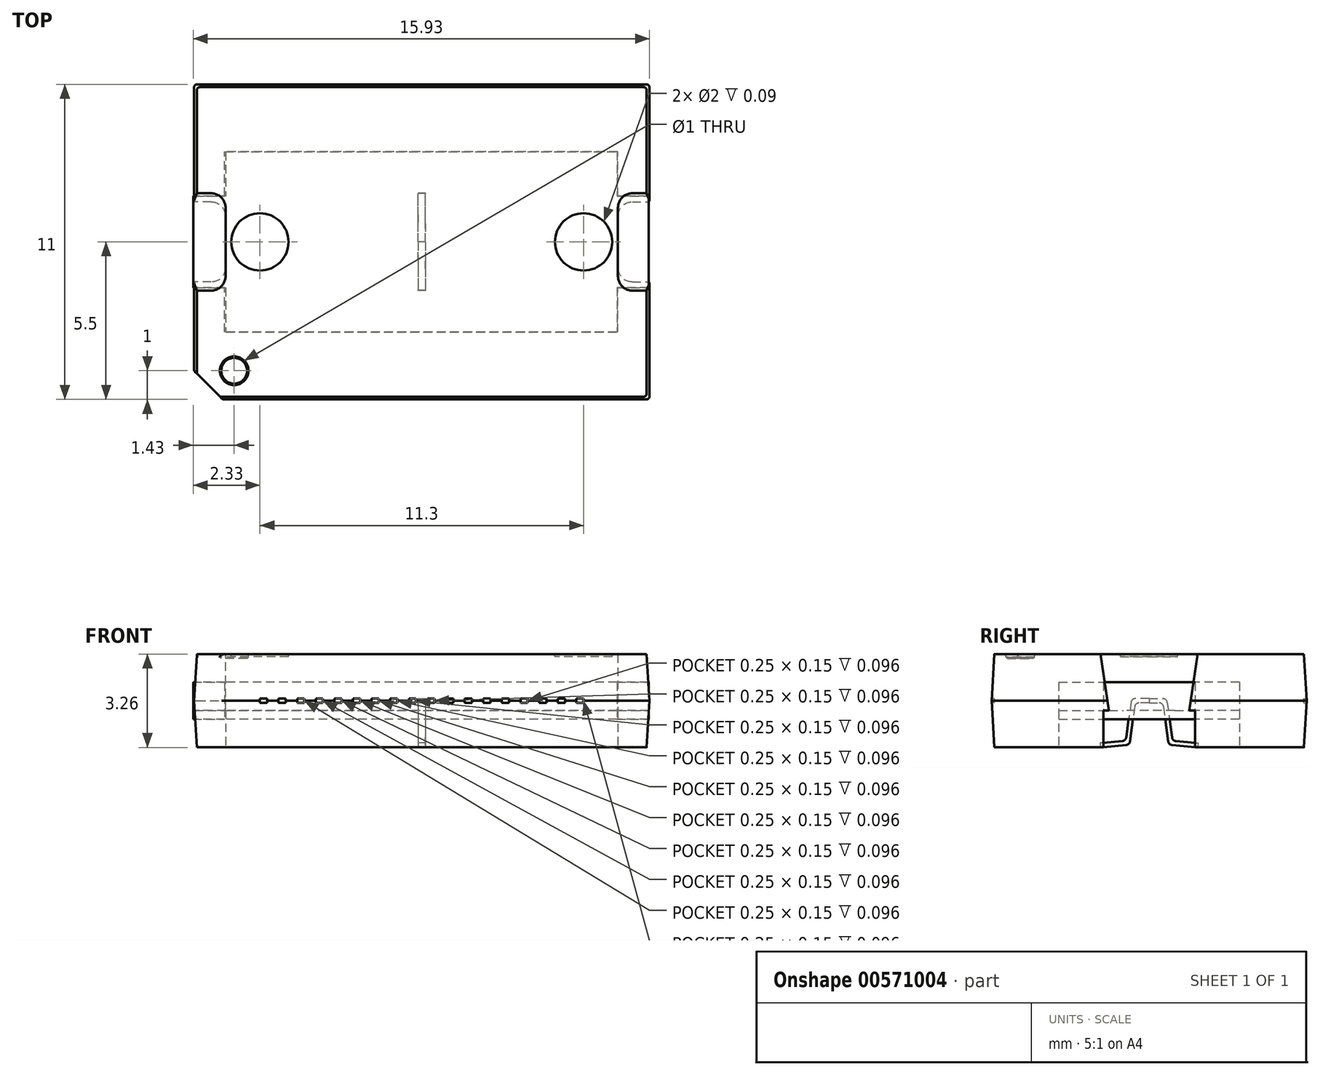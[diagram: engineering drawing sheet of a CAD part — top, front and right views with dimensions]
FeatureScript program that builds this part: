
annotation { "Feature Type Name" : "Feature", "Feature Type Description" : "" }
export const myFeature = defineFeature(function(context is Context, id is Id, definition is map)
    precondition{}
    {
        {
            var Q0;
            Q0=qCreatedBy(makeId("Top.planeOp"),FACE);
            var sketch = newSketch(context, id + "F0", { "sketchPlane" : qUnion([Q0])});
            skLineSegment(sketch, "E0.bottom", {"start": v(-7.95, 5.5) * mm, "end": v(7.95, 5.5) * mm});
            skLineSegment(sketch, "E0.top", {"start": v(-7.95, -5.5) * mm, "end": v(7.95, -5.5) * mm});
            skLineSegment(sketch, "E0.left", {"start": v(-7.95, 5.5) * mm, "end": v(-7.95, -5.5) * mm});
            skLineSegment(sketch, "E0.right", {"start": v(7.95, 5.5) * mm, "end": v(7.95, -5.5) * mm});
            skPoint(sketch, "E0.middle", {"position": v(0, 0) * mm});
            skLineSegment(sketch, "E1", {"start": v(-6.95, -5.5) * mm, "end": v(-7.95, -4.5) * mm});
            skLineSegment(sketch, "E2", {"start": v(-7.95, 1.4) * mm, "end": v(-6.85, 1.4) * mm});
            skLineSegment(sketch, "E3", {"start": v(-6.85, 1.4) * mm, "end": v(-6.85, -1.4) * mm});
            skLineSegment(sketch, "E4", {"start": v(-6.85, -1.4) * mm, "end": v(-7.95, -1.4) * mm});
            skLineSegment(sketch, "E5.MirrorCS", {"start": v(7.95, 1.4) * mm, "end": v(6.85, 1.4) * mm});
            skLineSegment(sketch, "E6.MirrorCS", {"start": v(6.85, 1.4) * mm, "end": v(6.85, -1.4) * mm});
            skLineSegment(sketch, "E7.MirrorCS", {"start": v(6.85, -1.4) * mm, "end": v(7.95, -1.4) * mm});
            skLineSegment(sketch, "E8", {"start": v(6.85, 2.95) * mm, "end": v(6.85, 1.6) * mm});
            skLineSegment(sketch, "E9", {"start": v(6.85, 2.95) * mm, "end": v(0, 2.95) * mm});
            skLineSegment(sketch, "E10", {"start": v(6.85, 1.6) * mm, "end": v(7.95, 1.6) * mm});
            skLineSegment(sketch, "E11", {"start": v(0, -2.95) * mm, "end": v(6.85, -2.95) * mm});
            skLineSegment(sketch, "E12", {"start": v(6.85, -2.95) * mm, "end": v(6.85, -1.6) * mm});
            skLineSegment(sketch, "E13", {"start": v(6.85, -1.6) * mm, "end": v(7.95, -1.6) * mm});
            skLineSegment(sketch, "E14.MirrorCS", {"start": v(-6.85, 2.95) * mm, "end": v(0, 2.95) * mm});
            skLineSegment(sketch, "E15.MirrorCS", {"start": v(-6.85, 2.95) * mm, "end": v(-6.85, 1.6) * mm});
            skLineSegment(sketch, "E16.MirrorCS", {"start": v(-6.85, 1.6) * mm, "end": v(-7.95, 1.6) * mm});
            skLineSegment(sketch, "E17.MirrorCS", {"start": v(0, -2.95) * mm, "end": v(-6.85, -2.95) * mm});
            skLineSegment(sketch, "E18.MirrorCS", {"start": v(-6.85, -1.6) * mm, "end": v(-7.95, -1.6) * mm});
            skLineSegment(sketch, "E19.MirrorCS", {"start": v(-6.85, -2.95) * mm, "end": v(-6.85, -1.6) * mm});
            skSolve(sketch);
        }
        {
            var Q0;
            {var subQ1=sQuery(id+"F0.wireOp",EDGE,"E0.bottom");Q0=makeQuery(id+"F0.imprint","IMPRINT",FACE,{"disambiguationData":[TD([[makeQuery(id+"F0.imprint","IMPRINT",EDGE,{"derivedFrom":subQ1}),-1.0]])]});}
            var Q1;
            {var subQ0=sQuery(id+"F0.wireOp",EDGE,"E1");Q1=makeQuery(id+"F0.imprint","IMPRINT",FACE,{"disambiguationData":[TD([[makeQuery(id+"F0.imprint","IMPRINT",EDGE,{"derivedFrom":subQ0}),-1.0]])]});}
            var Q2;
            {var subQ2=sQuery(id+"F0.wireOp",EDGE,"E2");Q2=makeQuery(id+"F0.imprint","IMPRINT",FACE,{"disambiguationData":[TD([[makeQuery(id+"F0.imprint","IMPRINT",EDGE,{"derivedFrom":subQ2}),1.0]])]});}
            var Q3;
            {var subQ0=sQuery(id+"F0.wireOp",EDGE,"E2");Q3=makeQuery(id+"F0.imprint","IMPRINT",FACE,{"disambiguationData":[TD([[makeQuery(id+"F0.imprint","IMPRINT",EDGE,{"derivedFrom":subQ0}),-1.0]])]});}
            var Q4;
            {var subQ0=sQuery(id+"F0.wireOp",EDGE,"E5.MirrorCS");Q4=makeQuery(id+"F0.imprint","IMPRINT",FACE,{"disambiguationData":[TD([[makeQuery(id+"F0.imprint","IMPRINT",EDGE,{"derivedFrom":subQ0}),1.0]])]});}
            extrude(context, id + "F1", {"entities" : qUnion([Q0, Q1, Q2, Q3, Q4]), "endBound" : BoundingType.SYMMETRIC, "depth" : 3.25 * mm, "offsetDistance" : 25 * mm});
        }
        {
            var Q0;
            Q0=makeQuery(id+"F1.opExtrude","CAP_FACE",FACE,{"disambiguationData":[OSD([sQuery(id+"F0.wireOp",EDGE,"E0.bottom"),sQuery(id+"F0.wireOp",EDGE,"E0.top"),sQuery(id+"F0.wireOp",EDGE,"E0.left"),sQuery(id+"F0.wireOp",EDGE,"E0.right"),sQuery(id+"F0.wireOp",EDGE,"E1")])],"isStart":true});
            var sketch = newSketch(context, id + "F2", { "sketchPlane" : qUnion([Q0])});
            skLineSegment(sketch, "E20", {"start": v(-6.85, -1.6) * mm, "end": v(-7.95, -1.6) * mm});
            skLineSegment(sketch, "E21", {"start": v(-7.95, -1.6) * mm, "end": v(-7.95, 1.6) * mm});
            skLineSegment(sketch, "E22", {"start": v(-7.95, 1.6) * mm, "end": v(-6.84, 1.6) * mm});
            skLineSegment(sketch, "E23", {"start": v(-6.84, 1.6) * mm, "end": v(-6.84, 3.15) * mm});
            skLineSegment(sketch, "E24", {"start": v(-6.84, 3.15) * mm, "end": v(0, 3.15) * mm});
            skLineSegment(sketch, "E25", {"start": v(0, 3.15) * mm, "end": v(6.85, 3.15) * mm});
            skPoint(sketch, "E25.endSnap0", {"position": v(-3.42, 3.15) * mm});
            skLineSegment(sketch, "E26", {"start": v(6.85, 3.15) * mm, "end": v(6.85, 1.6) * mm});
            skLineSegment(sketch, "E27", {"start": v(6.85, 1.6) * mm, "end": v(7.95, 1.6) * mm});
            skLineSegment(sketch, "E28", {"start": v(7.95, 1.6) * mm, "end": v(7.95, -1.6) * mm});
            skLineSegment(sketch, "E29", {"start": v(7.95, -1.6) * mm, "end": v(6.85, -1.6) * mm});
            skLineSegment(sketch, "E30", {"start": v(6.85, -1.6) * mm, "end": v(6.85, -3.15) * mm});
            skLineSegment(sketch, "E31", {"start": v(6.85, -3.15) * mm, "end": v(-6.85, -3.15) * mm});
            skLineSegment(sketch, "E32", {"start": v(-6.85, -3.15) * mm, "end": v(-6.85, -1.6) * mm});
            skSolve(sketch);
        }
        {
            var Q0;
            Q0=makeQuery(id+"F2.imprint","IMPRINT",FACE,{"disambiguationData":[TD([[makeQuery(id+"F2.imprint","IMPRINT",EDGE,{"derivedFrom":sQuery(id+"F2.wireOp",EDGE,"E20")}),-1.0]])]});
            extrude(context, id + "F3", {"entities" : qUnion([Q0]), "operationType" : NewBodyOperationType.REMOVE, "oppositeDirection" : true, "depth" : 1.29 * mm, "offsetDistance" : 25 * mm});
        }
        {
            var Q0;
            Q0=makeQuery(id+"F1.opExtrude","SWEPT_FACE",FACE,{"disambiguationData":[OSD([sQuery(id+"F0.wireOp",EDGE,"E0.right")])]});
            var sketch = newSketch(context, id + "F4", { "sketchPlane" : qUnion([Q0])});
            skLineSegment(sketch, "E33", {"start": v(0, -0.34) * mm, "end": v(0, 1.63) * mm});
            skLineSegment(sketch, "E34", {"start": v(0, 1.63) * mm, "end": v(-1.7, 1.63) * mm});
            skLineSegment(sketch, "E35", {"start": v(-1.7, 1.63) * mm, "end": v(-1.4, -0.34) * mm});
            skLineSegment(sketch, "E36", {"start": v(-1.4, -0.34) * mm, "end": v(0, -0.34) * mm});
            skLineSegment(sketch, "E37.MirrorCS", {"start": v(1.7, 1.63) * mm, "end": v(1.4, -0.34) * mm});
            skLineSegment(sketch, "E38.MirrorCS", {"start": v(0, 1.63) * mm, "end": v(1.7, 1.63) * mm});
            skLineSegment(sketch, "E39.MirrorCS", {"start": v(1.4, -0.34) * mm, "end": v(0, -0.34) * mm});
            skSolve(sketch);
        }
        {
            var Q0;
            Q0=makeQuery(id+"F4.imprint","IMPRINT",FACE,{"disambiguationData":[TD([[makeQuery(id+"F4.imprint","IMPRINT",EDGE,{"derivedFrom":sQuery(id+"F4.wireOp",EDGE,"E33")}),1.0]])]});
            var Q1;
            Q1=makeQuery(id+"F4.imprint","IMPRINT",FACE,{"disambiguationData":[TD([[makeQuery(id+"F4.imprint","IMPRINT",EDGE,{"derivedFrom":sQuery(id+"F4.wireOp",EDGE,"E33")}),-1.0]])]});
            extrude(context, id + "F5", {"entities" : qUnion([Q0, Q1]), "operationType" : NewBodyOperationType.REMOVE, "oppositeDirection" : true, "depth" : 1.1 * mm, "offsetDistance" : 25 * mm});
        }
        {
            var Q0;
            Q0=makeQuery(id+"F1.opExtrude","SWEPT_FACE",FACE,{"disambiguationData":[OSD([sQuery(id+"F0.wireOp",EDGE,"E0.left")])]});
            var sketch = newSketch(context, id + "F6", { "sketchPlane" : qUnion([Q0])});
            skLineSegment(sketch, "E40", {"start": v(0, -0.33) * mm, "end": v(-1.4, -0.34) * mm});
            skLineSegment(sketch, "E41", {"start": v(-1.4, -0.34) * mm, "end": v(-1.7, 1.63) * mm});
            skLineSegment(sketch, "E42", {"start": v(-1.7, 1.63) * mm, "end": v(0, 1.63) * mm});
            skLineSegment(sketch, "E43.MirrorCS", {"start": v(1.4, -0.34) * mm, "end": v(1.7, 1.63) * mm});
            skLineSegment(sketch, "E44.MirrorCS", {"start": v(1.7, 1.63) * mm, "end": v(0, 1.63) * mm});
            skLineSegment(sketch, "E45.MirrorCS", {"start": v(0, -0.33) * mm, "end": v(1.4, -0.34) * mm});
            skSolve(sketch);
        }
        {
            var Q0;
            Q0=makeQuery(id+"F6.imprint","IMPRINT",FACE,{"disambiguationData":[TD([[makeQuery(id+"F6.imprint","IMPRINT",EDGE,{"derivedFrom":sQuery(id+"F6.wireOp",EDGE,"E40")}),1.0]])]});
            extrude(context, id + "F7", {"entities" : qUnion([Q0]), "operationType" : NewBodyOperationType.REMOVE, "oppositeDirection" : true, "depth" : 1.1 * mm, "offsetDistance" : 25 * mm});
        }
        {
            var Q0;
            Q0=makeQuery(id+"F1.opExtrude","CAP_FACE",FACE,{"disambiguationData":[OSD([sQuery(id+"F0.wireOp",EDGE,"E0.bottom"),sQuery(id+"F0.wireOp",EDGE,"E0.top"),sQuery(id+"F0.wireOp",EDGE,"E0.left"),sQuery(id+"F0.wireOp",EDGE,"E0.right"),sQuery(id+"F0.wireOp",EDGE,"E1")])],"isStart":false});
            var sketch = newSketch(context, id + "F8", { "sketchPlane" : qUnion([Q0])});
            skCircle(sketch, "E46", {"center": v(-6.55, -4.5) * mm, "radius": 0.5 * mm});
            skCircle(sketch, "E47", {"center": v(-5.65, 0) * mm, "radius": 1 * mm});
            skPoint(sketch, "E47.centerSnap0", {"position": v(-6.85, 0) * mm});
            skCircle(sketch, "E48", {"center": v(5.65, 0) * mm, "radius": 1 * mm});
            skSolve(sketch);
        }
        {
            var Q0;
            Q0=makeQuery(id+"F8.imprint","IMPRINT",FACE,{"disambiguationData":[TD([[makeQuery(id+"F8.imprint","IMPRINT",EDGE,{"derivedFrom":sQuery(id+"F8.wireOp",EDGE,"E47")}),1.0]])]});
            var Q1;
            Q1=makeQuery(id+"F8.imprint","IMPRINT",FACE,{"disambiguationData":[TD([[makeQuery(id+"F8.imprint","IMPRINT",EDGE,{"derivedFrom":sQuery(id+"F8.wireOp",EDGE,"E48")}),1.0]])]});
            extrude(context, id + "F9", {"entities" : qUnion([Q0, Q1]), "operationType" : NewBodyOperationType.REMOVE, "oppositeDirection" : true, "depth" : 0.09 * mm, "offsetDistance" : 25 * mm});
        }
        {
            var Q0;
            Q0=makeQuery(id+"F1.opExtrude","SWEPT_FACE",FACE,{"disambiguationData":[OSD([sQuery(id+"F0.wireOp",EDGE,"E0.top")])]});
            var sketch = newSketch(context, id + "F10", { "sketchPlane" : qUnion([Q0])});
            skLineSegment(sketch, "E49.bottom", {"start": v(-0.45, 0.07) * mm, "end": v(-0.2, 0.07) * mm});
            skLineSegment(sketch, "E49.top", {"start": v(-0.45, -0.08) * mm, "end": v(-0.2, -0.08) * mm});
            skLineSegment(sketch, "E49.left", {"start": v(-0.45, 0.07) * mm, "end": v(-0.45, -0.08) * mm});
            skLineSegment(sketch, "E49.right", {"start": v(-0.2, 0.07) * mm, "end": v(-0.2, -0.08) * mm});
            skPoint(sketch, "E49.middle", {"position": v(-0.33, 0) * mm});
            skLineSegment(sketch, "E50.bottom", {"start": v(-1.1, 0.08) * mm, "end": v(-0.85, 0.08) * mm});
            skLineSegment(sketch, "E50.top", {"start": v(-1.1, -0.07) * mm, "end": v(-0.85, -0.07) * mm});
            skLineSegment(sketch, "E50.left", {"start": v(-1.1, 0.08) * mm, "end": v(-1.1, -0.07) * mm});
            skLineSegment(sketch, "E50.right", {"start": v(-0.85, 0.08) * mm, "end": v(-0.85, -0.07) * mm});
            skPoint(sketch, "E50.middle", {"position": v(-0.98, 0) * mm});
            skLineSegment(sketch, "E51.MirrorCS", {"start": v(0.2, 0.07) * mm, "end": v(0.2, -0.08) * mm});
            skLineSegment(sketch, "E52.MirrorCS", {"start": v(0.45, 0.07) * mm, "end": v(0.2, 0.07) * mm});
            skLineSegment(sketch, "E53.MirrorCS", {"start": v(0.45, 0.07) * mm, "end": v(0.45, -0.08) * mm});
            skLineSegment(sketch, "E54.MirrorCS", {"start": v(0.45, -0.08) * mm, "end": v(0.2, -0.08) * mm});
            skLineSegment(sketch, "E55.MirrorCS", {"start": v(0.85, 0.08) * mm, "end": v(0.85, -0.07) * mm});
            skLineSegment(sketch, "E56.MirrorCS", {"start": v(1.1, 0.08) * mm, "end": v(0.85, 0.08) * mm});
            skLineSegment(sketch, "E57.MirrorCS", {"start": v(1.1, 0.08) * mm, "end": v(1.1, -0.07) * mm});
            skLineSegment(sketch, "E58.MirrorCS", {"start": v(1.1, -0.07) * mm, "end": v(0.85, -0.07) * mm});
            skLineSegment(sketch, "E59.bottom", {"start": v(-1.75, 0.08) * mm, "end": v(-1.5, 0.08) * mm});
            skLineSegment(sketch, "E59.top", {"start": v(-1.75, -0.07) * mm, "end": v(-1.5, -0.07) * mm});
            skLineSegment(sketch, "E59.left", {"start": v(-1.75, 0.08) * mm, "end": v(-1.75, -0.07) * mm});
            skLineSegment(sketch, "E59.right", {"start": v(-1.5, 0.08) * mm, "end": v(-1.5, -0.07) * mm});
            skPoint(sketch, "E59.middle", {"position": v(-1.63, 0) * mm});
            skLineSegment(sketch, "E60.bottom", {"start": v(-2.4, 0.08) * mm, "end": v(-2.15, 0.08) * mm});
            skLineSegment(sketch, "E60.top", {"start": v(-2.4, -0.07) * mm, "end": v(-2.15, -0.07) * mm});
            skLineSegment(sketch, "E60.left", {"start": v(-2.4, 0.08) * mm, "end": v(-2.4, -0.07) * mm});
            skLineSegment(sketch, "E60.right", {"start": v(-2.15, 0.08) * mm, "end": v(-2.15, -0.07) * mm});
            skPoint(sketch, "E60.middle", {"position": v(-2.27, 0) * mm});
            skLineSegment(sketch, "E61.bottom", {"start": v(-3.05, 0.08) * mm, "end": v(-2.8, 0.08) * mm});
            skLineSegment(sketch, "E61.top", {"start": v(-3.05, -0.07) * mm, "end": v(-2.8, -0.07) * mm});
            skLineSegment(sketch, "E61.left", {"start": v(-3.05, 0.08) * mm, "end": v(-3.05, -0.07) * mm});
            skLineSegment(sketch, "E61.right", {"start": v(-2.8, 0.08) * mm, "end": v(-2.8, -0.07) * mm});
            skPoint(sketch, "E61.middle", {"position": v(-2.93, 0) * mm});
            skLineSegment(sketch, "E62.bottom", {"start": v(-3.45, -0.07) * mm, "end": v(-3.7, -0.07) * mm});
            skLineSegment(sketch, "E62.top", {"start": v(-3.45, 0.08) * mm, "end": v(-3.7, 0.08) * mm});
            skLineSegment(sketch, "E62.left", {"start": v(-3.45, -0.07) * mm, "end": v(-3.45, 0.08) * mm});
            skLineSegment(sketch, "E62.right", {"start": v(-3.7, -0.07) * mm, "end": v(-3.7, 0.08) * mm});
            skPoint(sketch, "E62.middle", {"position": v(-3.58, 0) * mm});
            skLineSegment(sketch, "E63.bottom", {"start": v(-4.1, -0.08) * mm, "end": v(-4.35, -0.08) * mm});
            skLineSegment(sketch, "E63.top", {"start": v(-4.1, 0.07) * mm, "end": v(-4.35, 0.07) * mm});
            skLineSegment(sketch, "E63.left", {"start": v(-4.1, -0.08) * mm, "end": v(-4.1, 0.07) * mm});
            skLineSegment(sketch, "E63.right", {"start": v(-4.35, -0.08) * mm, "end": v(-4.35, 0.07) * mm});
            skPoint(sketch, "E63.middle", {"position": v(-4.23, 0) * mm});
            skLineSegment(sketch, "E64.bottom", {"start": v(-4.75, -0.07) * mm, "end": v(-5, -0.07) * mm});
            skLineSegment(sketch, "E64.top", {"start": v(-4.75, 0.08) * mm, "end": v(-5, 0.08) * mm});
            skLineSegment(sketch, "E64.left", {"start": v(-4.75, -0.07) * mm, "end": v(-4.75, 0.08) * mm});
            skLineSegment(sketch, "E64.right", {"start": v(-5, -0.07) * mm, "end": v(-5, 0.08) * mm});
            skPoint(sketch, "E64.middle", {"position": v(-4.88, 0) * mm});
            skLineSegment(sketch, "E65.MirrorCS", {"start": v(5, -0.07) * mm, "end": v(5, 0.08) * mm});
            skLineSegment(sketch, "E66.MirrorCS", {"start": v(4.75, 0.08) * mm, "end": v(5, 0.08) * mm});
            skLineSegment(sketch, "E67.MirrorCS", {"start": v(4.75, -0.07) * mm, "end": v(5, -0.07) * mm});
            skLineSegment(sketch, "E68.MirrorCS", {"start": v(4.75, -0.07) * mm, "end": v(4.75, 0.08) * mm});
            skLineSegment(sketch, "E69.MirrorCS", {"start": v(4.35, -0.08) * mm, "end": v(4.35, 0.07) * mm});
            skLineSegment(sketch, "E70.MirrorCS", {"start": v(4.1, 0.07) * mm, "end": v(4.35, 0.07) * mm});
            skLineSegment(sketch, "E71.MirrorCS", {"start": v(4.1, -0.08) * mm, "end": v(4.35, -0.08) * mm});
            skLineSegment(sketch, "E72.MirrorCS", {"start": v(4.1, -0.08) * mm, "end": v(4.1, 0.07) * mm});
            skLineSegment(sketch, "E73.MirrorCS", {"start": v(3.7, -0.07) * mm, "end": v(3.7, 0.08) * mm});
            skLineSegment(sketch, "E74.MirrorCS", {"start": v(3.45, 0.08) * mm, "end": v(3.7, 0.08) * mm});
            skLineSegment(sketch, "E75.MirrorCS", {"start": v(3.45, -0.07) * mm, "end": v(3.45, 0.08) * mm});
            skLineSegment(sketch, "E76.MirrorCS", {"start": v(3.45, -0.07) * mm, "end": v(3.7, -0.07) * mm});
            skLineSegment(sketch, "E77.MirrorCS", {"start": v(3.05, 0.08) * mm, "end": v(3.05, -0.07) * mm});
            skLineSegment(sketch, "E78.MirrorCS", {"start": v(3.05, 0.08) * mm, "end": v(2.8, 0.08) * mm});
            skLineSegment(sketch, "E79.MirrorCS", {"start": v(2.8, 0.08) * mm, "end": v(2.8, -0.07) * mm});
            skLineSegment(sketch, "E80.MirrorCS", {"start": v(3.05, -0.07) * mm, "end": v(2.8, -0.07) * mm});
            skLineSegment(sketch, "E81.MirrorCS", {"start": v(2.4, 0.08) * mm, "end": v(2.4, -0.07) * mm});
            skLineSegment(sketch, "E82.MirrorCS", {"start": v(2.4, 0.08) * mm, "end": v(2.15, 0.08) * mm});
            skLineSegment(sketch, "E83.MirrorCS", {"start": v(2.15, 0.08) * mm, "end": v(2.15, -0.07) * mm});
            skLineSegment(sketch, "E84.MirrorCS", {"start": v(2.4, -0.07) * mm, "end": v(2.15, -0.07) * mm});
            skLineSegment(sketch, "E85.MirrorCS", {"start": v(1.75, 0.08) * mm, "end": v(1.75, -0.07) * mm});
            skLineSegment(sketch, "E86.MirrorCS", {"start": v(1.75, 0.08) * mm, "end": v(1.5, 0.08) * mm});
            skLineSegment(sketch, "E87.MirrorCS", {"start": v(1.75, -0.07) * mm, "end": v(1.5, -0.07) * mm});
            skLineSegment(sketch, "E88.MirrorCS", {"start": v(1.5, 0.08) * mm, "end": v(1.5, -0.07) * mm});
            skLineSegment(sketch, "E89.bottom", {"start": v(-5.65, 0.07) * mm, "end": v(-5.4, 0.07) * mm});
            skLineSegment(sketch, "E89.top", {"start": v(-5.65, -0.08) * mm, "end": v(-5.4, -0.08) * mm});
            skLineSegment(sketch, "E89.left", {"start": v(-5.65, 0.07) * mm, "end": v(-5.65, -0.08) * mm});
            skLineSegment(sketch, "E89.right", {"start": v(-5.4, 0.07) * mm, "end": v(-5.4, -0.08) * mm});
            skPoint(sketch, "E89.middle", {"position": v(-5.53, 0) * mm});
            skLineSegment(sketch, "E90.MirrorCS", {"start": v(5.65, 0.07) * mm, "end": v(5.65, -0.08) * mm});
            skLineSegment(sketch, "E91.MirrorCS", {"start": v(5.65, 0.07) * mm, "end": v(5.4, 0.07) * mm});
            skLineSegment(sketch, "E92.MirrorCS", {"start": v(5.4, 0.07) * mm, "end": v(5.4, -0.08) * mm});
            skLineSegment(sketch, "E93.MirrorCS", {"start": v(5.65, -0.08) * mm, "end": v(5.4, -0.08) * mm});
            skSolve(sketch);
        }
        {
            var Q0;
            Q0=makeQuery(id+"F10.imprint","IMPRINT",FACE,{"disambiguationData":[TD([[makeQuery(id+"F10.imprint","IMPRINT",EDGE,{"derivedFrom":sQuery(id+"F10.wireOp",EDGE,"E64.bottom")}),-1.0]])]});
            var Q1;
            Q1=makeQuery(id+"F10.imprint","IMPRINT",FACE,{"disambiguationData":[TD([[makeQuery(id+"F10.imprint","IMPRINT",EDGE,{"derivedFrom":sQuery(id+"F10.wireOp",EDGE,"E63.bottom")}),-1.0]])]});
            var Q2;
            Q2=makeQuery(id+"F10.imprint","IMPRINT",FACE,{"disambiguationData":[TD([[makeQuery(id+"F10.imprint","IMPRINT",EDGE,{"derivedFrom":sQuery(id+"F10.wireOp",EDGE,"E62.bottom")}),-1.0]])]});
            var Q3;
            Q3=makeQuery(id+"F10.imprint","IMPRINT",FACE,{"disambiguationData":[TD([[makeQuery(id+"F10.imprint","IMPRINT",EDGE,{"derivedFrom":sQuery(id+"F10.wireOp",EDGE,"E61.bottom")}),-1.0]])]});
            var Q4;
            Q4=makeQuery(id+"F10.imprint","IMPRINT",FACE,{"disambiguationData":[TD([[makeQuery(id+"F10.imprint","IMPRINT",EDGE,{"derivedFrom":sQuery(id+"F10.wireOp",EDGE,"E60.bottom")}),-1.0]])]});
            var Q5;
            Q5=makeQuery(id+"F10.imprint","IMPRINT",FACE,{"disambiguationData":[TD([[makeQuery(id+"F10.imprint","IMPRINT",EDGE,{"derivedFrom":sQuery(id+"F10.wireOp",EDGE,"E59.bottom")}),-1.0]])]});
            var Q6;
            Q6=makeQuery(id+"F10.imprint","IMPRINT",FACE,{"disambiguationData":[TD([[makeQuery(id+"F10.imprint","IMPRINT",EDGE,{"derivedFrom":sQuery(id+"F10.wireOp",EDGE,"E50.bottom")}),-1.0]])]});
            var Q7;
            Q7=makeQuery(id+"F10.imprint","IMPRINT",FACE,{"disambiguationData":[TD([[makeQuery(id+"F10.imprint","IMPRINT",EDGE,{"derivedFrom":sQuery(id+"F10.wireOp",EDGE,"E49.bottom")}),-1.0]])]});
            var Q8;
            Q8=makeQuery(id+"F10.imprint","IMPRINT",FACE,{"disambiguationData":[TD([[makeQuery(id+"F10.imprint","IMPRINT",EDGE,{"derivedFrom":sQuery(id+"F10.wireOp",EDGE,"E51.MirrorCS")}),1.0]])]});
            var Q9;
            Q9=makeQuery(id+"F10.imprint","IMPRINT",FACE,{"disambiguationData":[TD([[makeQuery(id+"F10.imprint","IMPRINT",EDGE,{"derivedFrom":sQuery(id+"F10.wireOp",EDGE,"E55.MirrorCS")}),1.0]])]});
            var Q10;
            Q10=makeQuery(id+"F10.imprint","IMPRINT",FACE,{"disambiguationData":[TD([[makeQuery(id+"F10.imprint","IMPRINT",EDGE,{"derivedFrom":sQuery(id+"F10.wireOp",EDGE,"E85.MirrorCS")}),-1.0]])]});
            var Q11;
            Q11=makeQuery(id+"F10.imprint","IMPRINT",FACE,{"disambiguationData":[TD([[makeQuery(id+"F10.imprint","IMPRINT",EDGE,{"derivedFrom":sQuery(id+"F10.wireOp",EDGE,"E81.MirrorCS")}),-1.0]])]});
            var Q12;
            Q12=makeQuery(id+"F10.imprint","IMPRINT",FACE,{"disambiguationData":[TD([[makeQuery(id+"F10.imprint","IMPRINT",EDGE,{"derivedFrom":sQuery(id+"F10.wireOp",EDGE,"E77.MirrorCS")}),-1.0]])]});
            var Q13;
            Q13=makeQuery(id+"F10.imprint","IMPRINT",FACE,{"disambiguationData":[TD([[makeQuery(id+"F10.imprint","IMPRINT",EDGE,{"derivedFrom":sQuery(id+"F10.wireOp",EDGE,"E73.MirrorCS")}),1.0]])]});
            var Q14;
            Q14=makeQuery(id+"F10.imprint","IMPRINT",FACE,{"disambiguationData":[TD([[makeQuery(id+"F10.imprint","IMPRINT",EDGE,{"derivedFrom":sQuery(id+"F10.wireOp",EDGE,"E69.MirrorCS")}),1.0]])]});
            var Q15;
            Q15=makeQuery(id+"F10.imprint","IMPRINT",FACE,{"disambiguationData":[TD([[makeQuery(id+"F10.imprint","IMPRINT",EDGE,{"derivedFrom":sQuery(id+"F10.wireOp",EDGE,"E65.MirrorCS")}),1.0]])]});
            var Q16;
            Q16=makeQuery(id+"F10.imprint","IMPRINT",FACE,{"disambiguationData":[TD([[makeQuery(id+"F10.imprint","IMPRINT",EDGE,{"derivedFrom":sQuery(id+"F10.wireOp",EDGE,"E89.bottom")}),-1.0]])]});
            var Q17;
            Q17=makeQuery(id+"F10.imprint","IMPRINT",FACE,{"disambiguationData":[TD([[makeQuery(id+"F10.imprint","IMPRINT",EDGE,{"derivedFrom":sQuery(id+"F10.wireOp",EDGE,"E90.MirrorCS")}),-1.0]])]});
            extrude(context, id + "F11", {"entities" : qUnion([Q0, Q1, Q2, Q3, Q4, Q5, Q6, Q7, Q8, Q9, Q10, Q11, Q12, Q13, Q14, Q15, Q16, Q17]), "operationType" : NewBodyOperationType.REMOVE, "oppositeDirection" : true, "depth" : 0.1 * mm, "offsetDistance" : 25 * mm});
        }
        {
            var Q0;
            Q0=makeQuery(id+"F1.opExtrude","SWEPT_FACE",FACE,{"disambiguationData":[OSD([sQuery(id+"F0.wireOp",EDGE,"E0.bottom")])]});
            var sketch = newSketch(context, id + "F12", { "sketchPlane" : qUnion([Q0])});
            skLineSegment(sketch, "E94.bottom", {"start": v(-0.2, -0.08) * mm, "end": v(-0.45, -0.08) * mm});
            skLineSegment(sketch, "E94.top", {"start": v(-0.2, 0.07) * mm, "end": v(-0.45, 0.07) * mm});
            skLineSegment(sketch, "E94.left", {"start": v(-0.2, -0.08) * mm, "end": v(-0.2, 0.07) * mm});
            skLineSegment(sketch, "E94.right", {"start": v(-0.45, -0.08) * mm, "end": v(-0.45, 0.07) * mm});
            skPoint(sketch, "E94.middle", {"position": v(-0.33, 0) * mm});
            skLineSegment(sketch, "E95.bottom", {"start": v(-1.5, -0.07) * mm, "end": v(-1.75, -0.07) * mm});
            skLineSegment(sketch, "E95.top", {"start": v(-1.5, 0.08) * mm, "end": v(-1.75, 0.08) * mm});
            skLineSegment(sketch, "E95.left", {"start": v(-1.5, -0.07) * mm, "end": v(-1.5, 0.08) * mm});
            skLineSegment(sketch, "E95.right", {"start": v(-1.75, -0.07) * mm, "end": v(-1.75, 0.08) * mm});
            skPoint(sketch, "E95.middle", {"position": v(-1.63, 0) * mm});
            skLineSegment(sketch, "E96.bottom", {"start": v(-0.85, -0.07) * mm, "end": v(-1.1, -0.07) * mm});
            skLineSegment(sketch, "E96.top", {"start": v(-0.85, 0.08) * mm, "end": v(-1.1, 0.08) * mm});
            skLineSegment(sketch, "E96.left", {"start": v(-0.85, -0.08) * mm, "end": v(-0.85, 0.08) * mm});
            skLineSegment(sketch, "E96.right", {"start": v(-1.1, -0.08) * mm, "end": v(-1.1, 0.07) * mm});
            skPoint(sketch, "E96.middle", {"position": v(-0.98, 0) * mm});
            skLineSegment(sketch, "E97.bottom", {"start": v(-2.15, -0.07) * mm, "end": v(-2.4, -0.08) * mm});
            skLineSegment(sketch, "E97.top", {"start": v(-2.15, 0.08) * mm, "end": v(-2.4, 0.07) * mm});
            skLineSegment(sketch, "E97.left", {"start": v(-2.15, -0.07) * mm, "end": v(-2.15, 0.08) * mm});
            skLineSegment(sketch, "E97.right", {"start": v(-2.4, -0.08) * mm, "end": v(-2.4, 0.07) * mm});
            skPoint(sketch, "E97.middle", {"position": v(-2.27, 0) * mm});
            skLineSegment(sketch, "E98.bottom", {"start": v(-3.05, 0.08) * mm, "end": v(-2.8, 0.08) * mm});
            skLineSegment(sketch, "E98.top", {"start": v(-3.05, -0.07) * mm, "end": v(-2.8, -0.07) * mm});
            skLineSegment(sketch, "E98.left", {"start": v(-3.05, 0.08) * mm, "end": v(-3.05, -0.07) * mm});
            skLineSegment(sketch, "E98.right", {"start": v(-2.8, 0.08) * mm, "end": v(-2.8, -0.07) * mm});
            skPoint(sketch, "E98.middle", {"position": v(-2.93, 0) * mm});
            skLineSegment(sketch, "E99.bottom", {"start": v(-3.7, 0.07) * mm, "end": v(-3.45, 0.07) * mm});
            skLineSegment(sketch, "E99.top", {"start": v(-3.7, -0.08) * mm, "end": v(-3.45, -0.08) * mm});
            skLineSegment(sketch, "E99.left", {"start": v(-3.7, 0.07) * mm, "end": v(-3.7, -0.08) * mm});
            skLineSegment(sketch, "E99.right", {"start": v(-3.45, 0.07) * mm, "end": v(-3.45, -0.08) * mm});
            skPoint(sketch, "E99.middle", {"position": v(-3.58, 0) * mm});
            skLineSegment(sketch, "E100.bottom", {"start": v(-4.35, 0.07) * mm, "end": v(-4.1, 0.07) * mm});
            skLineSegment(sketch, "E100.top", {"start": v(-4.35, -0.08) * mm, "end": v(-4.1, -0.08) * mm});
            skLineSegment(sketch, "E100.left", {"start": v(-4.35, 0.07) * mm, "end": v(-4.35, -0.08) * mm});
            skLineSegment(sketch, "E100.right", {"start": v(-4.1, 0.07) * mm, "end": v(-4.1, -0.08) * mm});
            skPoint(sketch, "E100.middle", {"position": v(-4.23, 0) * mm});
            skLineSegment(sketch, "E101.bottom", {"start": v(-4.75, -0.08) * mm, "end": v(-5, -0.08) * mm});
            skLineSegment(sketch, "E101.top", {"start": v(-4.75, 0.07) * mm, "end": v(-5, 0.07) * mm});
            skLineSegment(sketch, "E101.left", {"start": v(-4.75, -0.08) * mm, "end": v(-4.75, 0.07) * mm});
            skLineSegment(sketch, "E101.right", {"start": v(-5, -0.08) * mm, "end": v(-5, 0.07) * mm});
            skPoint(sketch, "E101.middle", {"position": v(-4.88, 0) * mm});
            skLineSegment(sketch, "E102.MirrorCS", {"start": v(0.2, -0.08) * mm, "end": v(0.45, -0.08) * mm});
            skLineSegment(sketch, "E103.MirrorCS", {"start": v(0.45, -0.08) * mm, "end": v(0.45, 0.07) * mm});
            skLineSegment(sketch, "E104.MirrorCS", {"start": v(0.2, 0.07) * mm, "end": v(0.45, 0.07) * mm});
            skLineSegment(sketch, "E105.MirrorCS", {"start": v(0.2, -0.08) * mm, "end": v(0.2, 0.07) * mm});
            skLineSegment(sketch, "E106.MirrorCS", {"start": v(0.85, -0.08) * mm, "end": v(0.85, 0.08) * mm});
            skLineSegment(sketch, "E107.MirrorCS", {"start": v(0.85, 0.08) * mm, "end": v(1.1, 0.08) * mm});
            skLineSegment(sketch, "E108.MirrorCS", {"start": v(1.1, -0.08) * mm, "end": v(1.1, 0.07) * mm});
            skLineSegment(sketch, "E109.MirrorCS", {"start": v(0.85, -0.07) * mm, "end": v(1.1, -0.07) * mm});
            skLineSegment(sketch, "E110.MirrorCS", {"start": v(1.5, -0.07) * mm, "end": v(1.5, 0.08) * mm});
            skLineSegment(sketch, "E111.MirrorCS", {"start": v(1.5, 0.08) * mm, "end": v(1.75, 0.08) * mm});
            skLineSegment(sketch, "E112.MirrorCS", {"start": v(1.75, -0.07) * mm, "end": v(1.75, 0.08) * mm});
            skLineSegment(sketch, "E113.MirrorCS", {"start": v(1.5, -0.07) * mm, "end": v(1.75, -0.07) * mm});
            skLineSegment(sketch, "E114.MirrorCS", {"start": v(2.15, -0.07) * mm, "end": v(2.15, 0.08) * mm});
            skLineSegment(sketch, "E115.MirrorCS", {"start": v(2.15, 0.08) * mm, "end": v(2.4, 0.07) * mm});
            skLineSegment(sketch, "E116.MirrorCS", {"start": v(2.4, -0.08) * mm, "end": v(2.4, 0.07) * mm});
            skLineSegment(sketch, "E117.MirrorCS", {"start": v(2.15, -0.07) * mm, "end": v(2.4, -0.08) * mm});
            skLineSegment(sketch, "E118.MirrorCS", {"start": v(2.8, 0.08) * mm, "end": v(2.8, -0.07) * mm});
            skLineSegment(sketch, "E119.MirrorCS", {"start": v(3.05, 0.08) * mm, "end": v(2.8, 0.08) * mm});
            skLineSegment(sketch, "E120.MirrorCS", {"start": v(3.05, 0.08) * mm, "end": v(3.05, -0.07) * mm});
            skLineSegment(sketch, "E121.MirrorCS", {"start": v(3.05, -0.07) * mm, "end": v(2.8, -0.07) * mm});
            skLineSegment(sketch, "E122.MirrorCS", {"start": v(3.45, 0.07) * mm, "end": v(3.45, -0.08) * mm});
            skLineSegment(sketch, "E123.MirrorCS", {"start": v(3.7, 0.07) * mm, "end": v(3.45, 0.07) * mm});
            skLineSegment(sketch, "E124.MirrorCS", {"start": v(3.7, 0.07) * mm, "end": v(3.7, -0.08) * mm});
            skLineSegment(sketch, "E125.MirrorCS", {"start": v(3.7, -0.08) * mm, "end": v(3.45, -0.08) * mm});
            skLineSegment(sketch, "E126.MirrorCS", {"start": v(4.1, 0.07) * mm, "end": v(4.1, -0.08) * mm});
            skLineSegment(sketch, "E127.MirrorCS", {"start": v(4.35, 0.07) * mm, "end": v(4.1, 0.07) * mm});
            skLineSegment(sketch, "E128.MirrorCS", {"start": v(4.35, 0.07) * mm, "end": v(4.35, -0.08) * mm});
            skLineSegment(sketch, "E129.MirrorCS", {"start": v(4.35, -0.08) * mm, "end": v(4.1, -0.08) * mm});
            skLineSegment(sketch, "E130.MirrorCS", {"start": v(4.75, -0.08) * mm, "end": v(4.75, 0.07) * mm});
            skLineSegment(sketch, "E131.MirrorCS", {"start": v(4.75, 0.07) * mm, "end": v(5, 0.07) * mm});
            skLineSegment(sketch, "E132.MirrorCS", {"start": v(5, -0.08) * mm, "end": v(5, 0.07) * mm});
            skLineSegment(sketch, "E133.MirrorCS", {"start": v(4.75, -0.08) * mm, "end": v(5, -0.08) * mm});
            skLineSegment(sketch, "E134", {"start": v(-7.95, 0) * mm, "end": v(-7.85, 1.63) * mm});
            skLineSegment(sketch, "E135.MirrorCS", {"start": v(-7.95, 0) * mm, "end": v(-7.85, -1.63) * mm});
            skLineSegment(sketch, "E136.MirrorCS", {"start": v(7.95, 0) * mm, "end": v(7.85, 1.63) * mm});
            skLineSegment(sketch, "E137.MirrorCS", {"start": v(7.95, 0) * mm, "end": v(7.85, -1.63) * mm});
            skLineSegment(sketch, "E138", {"start": v(-7.85, 1.63) * mm, "end": v(-7.95, 1.63) * mm});
            skLineSegment(sketch, "E139", {"start": v(-7.95, 1.63) * mm, "end": v(-7.95, 0) * mm});
            skLineSegment(sketch, "E140.MirrorCS", {"start": v(-7.95, -1.63) * mm, "end": v(-7.95, 0) * mm});
            skLineSegment(sketch, "E141.MirrorCS", {"start": v(-7.85, -1.63) * mm, "end": v(-7.95, -1.63) * mm});
            skLineSegment(sketch, "E142.MirrorCS", {"start": v(7.95, 1.63) * mm, "end": v(7.95, 0) * mm});
            skLineSegment(sketch, "E143.MirrorCS", {"start": v(7.85, 1.63) * mm, "end": v(7.95, 1.63) * mm});
            skLineSegment(sketch, "E144.MirrorCS", {"start": v(7.95, -1.63) * mm, "end": v(7.95, 0) * mm});
            skLineSegment(sketch, "E145.MirrorCS", {"start": v(7.85, -1.63) * mm, "end": v(7.95, -1.63) * mm});
            skLineSegment(sketch, "E146.bottom", {"start": v(-5.4, -0.08) * mm, "end": v(-5.65, -0.08) * mm});
            skLineSegment(sketch, "E146.top", {"start": v(-5.4, 0.07) * mm, "end": v(-5.65, 0.07) * mm});
            skLineSegment(sketch, "E146.left", {"start": v(-5.4, -0.08) * mm, "end": v(-5.4, 0.07) * mm});
            skLineSegment(sketch, "E146.right", {"start": v(-5.65, -0.08) * mm, "end": v(-5.65, 0.07) * mm});
            skPoint(sketch, "E146.middle", {"position": v(-5.53, 0) * mm});
            skLineSegment(sketch, "E147.MirrorCS", {"start": v(5.4, 0.07) * mm, "end": v(5.65, 0.07) * mm});
            skLineSegment(sketch, "E148.MirrorCS", {"start": v(5.65, -0.08) * mm, "end": v(5.65, 0.07) * mm});
            skLineSegment(sketch, "E149.MirrorCS", {"start": v(5.4, -0.08) * mm, "end": v(5.65, -0.08) * mm});
            skLineSegment(sketch, "E150.MirrorCS", {"start": v(5.4, -0.08) * mm, "end": v(5.4, 0.07) * mm});
            skSolve(sketch);
        }
        {
            var Q0;
            Q0=makeQuery(id+"F12.imprint","IMPRINT",FACE,{"disambiguationData":[TD([[makeQuery(id+"F12.imprint","IMPRINT",EDGE,{"derivedFrom":sQuery(id+"F12.wireOp",EDGE,"E101.bottom")}),-1.0]])]});
            var Q1;
            Q1=makeQuery(id+"F12.imprint","IMPRINT",FACE,{"disambiguationData":[TD([[makeQuery(id+"F12.imprint","IMPRINT",EDGE,{"derivedFrom":sQuery(id+"F12.wireOp",EDGE,"E100.bottom")}),-1.0]])]});
            var Q2;
            Q2=makeQuery(id+"F12.imprint","IMPRINT",FACE,{"disambiguationData":[TD([[makeQuery(id+"F12.imprint","IMPRINT",EDGE,{"derivedFrom":sQuery(id+"F12.wireOp",EDGE,"E99.bottom")}),-1.0]])]});
            var Q3;
            Q3=makeQuery(id+"F12.imprint","IMPRINT",FACE,{"disambiguationData":[TD([[makeQuery(id+"F12.imprint","IMPRINT",EDGE,{"derivedFrom":sQuery(id+"F12.wireOp",EDGE,"E98.bottom")}),-1.0]])]});
            var Q4;
            Q4=makeQuery(id+"F12.imprint","IMPRINT",FACE,{"disambiguationData":[TD([[makeQuery(id+"F12.imprint","IMPRINT",EDGE,{"derivedFrom":sQuery(id+"F12.wireOp",EDGE,"E97.bottom")}),-1.0]])]});
            var Q5;
            Q5=makeQuery(id+"F12.imprint","IMPRINT",FACE,{"disambiguationData":[TD([[makeQuery(id+"F12.imprint","IMPRINT",EDGE,{"derivedFrom":sQuery(id+"F12.wireOp",EDGE,"E95.bottom")}),-1.0]])]});
            var Q6;
            Q6=makeQuery(id+"F12.imprint","IMPRINT",FACE,{"disambiguationData":[TD([[makeQuery(id+"F12.imprint","IMPRINT",EDGE,{"derivedFrom":sQuery(id+"F12.wireOp",EDGE,"E96.bottom")}),-1.0]])]});
            var Q7;
            Q7=makeQuery(id+"F12.imprint","IMPRINT",FACE,{"disambiguationData":[TD([[makeQuery(id+"F12.imprint","IMPRINT",EDGE,{"derivedFrom":sQuery(id+"F12.wireOp",EDGE,"E94.bottom")}),-1.0]])]});
            var Q8;
            Q8=makeQuery(id+"F12.imprint","IMPRINT",FACE,{"disambiguationData":[TD([[makeQuery(id+"F12.imprint","IMPRINT",EDGE,{"derivedFrom":sQuery(id+"F12.wireOp",EDGE,"E102.MirrorCS")}),1.0]])]});
            var Q9;
            Q9=makeQuery(id+"F12.imprint","IMPRINT",FACE,{"disambiguationData":[TD([[makeQuery(id+"F12.imprint","IMPRINT",EDGE,{"derivedFrom":sQuery(id+"F12.wireOp",EDGE,"E106.MirrorCS")}),-1.0]])]});
            var Q10;
            Q10=makeQuery(id+"F12.imprint","IMPRINT",FACE,{"disambiguationData":[TD([[makeQuery(id+"F12.imprint","IMPRINT",EDGE,{"derivedFrom":sQuery(id+"F12.wireOp",EDGE,"E110.MirrorCS")}),-1.0]])]});
            var Q11;
            Q11=makeQuery(id+"F12.imprint","IMPRINT",FACE,{"disambiguationData":[TD([[makeQuery(id+"F12.imprint","IMPRINT",EDGE,{"derivedFrom":sQuery(id+"F12.wireOp",EDGE,"E118.MirrorCS")}),1.0]])]});
            var Q12;
            Q12=makeQuery(id+"F12.imprint","IMPRINT",FACE,{"disambiguationData":[TD([[makeQuery(id+"F12.imprint","IMPRINT",EDGE,{"derivedFrom":sQuery(id+"F12.wireOp",EDGE,"E122.MirrorCS")}),1.0]])]});
            var Q13;
            Q13=makeQuery(id+"F12.imprint","IMPRINT",FACE,{"disambiguationData":[TD([[makeQuery(id+"F12.imprint","IMPRINT",EDGE,{"derivedFrom":sQuery(id+"F12.wireOp",EDGE,"E126.MirrorCS")}),1.0]])]});
            var Q14;
            Q14=makeQuery(id+"F12.imprint","IMPRINT",FACE,{"disambiguationData":[TD([[makeQuery(id+"F12.imprint","IMPRINT",EDGE,{"derivedFrom":sQuery(id+"F12.wireOp",EDGE,"E130.MirrorCS")}),-1.0]])]});
            var Q15;
            Q15=makeQuery(id+"F12.imprint","IMPRINT",FACE,{"disambiguationData":[TD([[makeQuery(id+"F12.imprint","IMPRINT",EDGE,{"derivedFrom":sQuery(id+"F12.wireOp",EDGE,"E114.MirrorCS")}),-1.0]])]});
            var Q16;
            Q16=makeQuery(id+"F12.imprint","IMPRINT",FACE,{"disambiguationData":[TD([[makeQuery(id+"F12.imprint","IMPRINT",EDGE,{"derivedFrom":sQuery(id+"F12.wireOp",EDGE,"E146.bottom")}),-1.0]])]});
            var Q17;
            Q17=makeQuery(id+"F12.imprint","IMPRINT",FACE,{"disambiguationData":[TD([[makeQuery(id+"F12.imprint","IMPRINT",EDGE,{"derivedFrom":sQuery(id+"F12.wireOp",EDGE,"E147.MirrorCS")}),-1.0]])]});
            extrude(context, id + "F13", {"entities" : qUnion([Q0, Q1, Q2, Q3, Q4, Q5, Q6, Q7, Q8, Q9, Q10, Q11, Q12, Q13, Q14, Q15, Q16, Q17]), "operationType" : NewBodyOperationType.REMOVE, "oppositeDirection" : true, "depth" : 0.1 * mm, "offsetDistance" : 25 * mm});
        }
        {
            var Q0;
            Q0=makeQuery(id+"F12.imprint","IMPRINT",FACE,{"disambiguationData":[TD([[makeQuery(id+"F12.imprint","IMPRINT",EDGE,{"derivedFrom":sQuery(id+"F12.wireOp",EDGE,"E134")}),1.0]])]});
            var Q1;
            Q1=makeQuery(id+"F12.imprint","IMPRINT",FACE,{"disambiguationData":[TD([[makeQuery(id+"F12.imprint","IMPRINT",EDGE,{"derivedFrom":sQuery(id+"F12.wireOp",EDGE,"E135.MirrorCS")}),-1.0]])]});
            var Q2;
            Q2=makeQuery(id+"F12.imprint","IMPRINT",FACE,{"disambiguationData":[TD([[makeQuery(id+"F12.imprint","IMPRINT",EDGE,{"derivedFrom":sQuery(id+"F12.wireOp",EDGE,"E136.MirrorCS")}),-1.0]])]});
            var Q3;
            Q3=makeQuery(id+"F12.imprint","IMPRINT",FACE,{"disambiguationData":[TD([[makeQuery(id+"F12.imprint","IMPRINT",EDGE,{"derivedFrom":sQuery(id+"F12.wireOp",EDGE,"E137.MirrorCS")}),1.0]])]});
            extrude(context, id + "F14", {"entities" : qUnion([Q0, Q1, Q2, Q3]), "operationType" : NewBodyOperationType.REMOVE, "oppositeDirection" : true, "depth" : 15 * mm, "offsetDistance" : 25 * mm});
        }
        {
            var Q0;
            {var subQ6=sQuery(id+"F4.wireOp",EDGE,"E35");Q0=makeQuery(id+"F4.imprint","IMPRINT",FACE,{"disambiguationData":[TD([[makeQuery(id+"F4.imprint","IMPRINT",EDGE,{"derivedFrom":subQ6}),-1.0]])]});}
            var sketch = newSketch(context, id + "F15", { "sketchPlane" : qUnion([Q0])});
            skLineSegment(sketch, "E151", {"start": v(-5.5, 0) * mm, "end": v(-5.5, 1.63) * mm});
            skLineSegment(sketch, "E152", {"start": v(-5.5, 1.63) * mm, "end": v(-5.4, 1.63) * mm});
            skLineSegment(sketch, "E153", {"start": v(-5.4, 1.63) * mm, "end": v(-5.5, 0) * mm});
            skLineSegment(sketch, "E154.MirrorCS", {"start": v(-5.5, 0) * mm, "end": v(-5.5, -1.63) * mm});
            skLineSegment(sketch, "E155.MirrorCS", {"start": v(-5.5, -1.63) * mm, "end": v(-5.4, -1.63) * mm});
            skLineSegment(sketch, "E156.MirrorCS", {"start": v(-5.4, -1.63) * mm, "end": v(-5.5, 0) * mm});
            skLineSegment(sketch, "E157.MirrorCS", {"start": v(5.4, 1.63) * mm, "end": v(5.5, 0) * mm});
            skLineSegment(sketch, "E158.MirrorCS", {"start": v(5.5, 1.63) * mm, "end": v(5.4, 1.63) * mm});
            skLineSegment(sketch, "E159.MirrorCS", {"start": v(5.5, 0) * mm, "end": v(5.5, 1.63) * mm});
            skLineSegment(sketch, "E160.MirrorCS", {"start": v(5.4, -1.63) * mm, "end": v(5.5, 0) * mm});
            skLineSegment(sketch, "E161.MirrorCS", {"start": v(5.5, -1.63) * mm, "end": v(5.4, -1.63) * mm});
            skLineSegment(sketch, "E162.MirrorCS", {"start": v(5.5, 0) * mm, "end": v(5.5, -1.63) * mm});
            skSolve(sketch);
        }
        {
            var Q0;
            Q0 = qSketchRegion(id + "F15", true);
            extrude(context, id + "F16", {"entities" : qUnion([Q0]), "operationType" : NewBodyOperationType.REMOVE, "oppositeDirection" : true, "depth" : 25 * mm, "offsetDistance" : 25 * mm});
        }
        {
            var Q0;
            Q0=qCreatedBy(makeId("Top.planeOp"),FACE);
            var sketch = newSketch(context, id + "F17", { "sketchPlane" : qUnion([Q0])});
            skLineSegment(sketch, "E163", {"start": v(-7.98, 1.6) * mm, "end": v(-6.88, 1.6) * mm});
            skLineSegment(sketch, "E164", {"start": v(-6.88, 1.6) * mm, "end": v(-6.88, 3.15) * mm});
            skLineSegment(sketch, "E165", {"start": v(-6.88, 3.15) * mm, "end": v(6.82, 3.15) * mm});
            skLineSegment(sketch, "E166", {"start": v(6.82, 3.15) * mm, "end": v(6.82, 1.6) * mm});
            skLineSegment(sketch, "E167", {"start": v(6.82, 1.6) * mm, "end": v(7.92, 1.6) * mm});
            skLineSegment(sketch, "E168", {"start": v(7.92, 1.6) * mm, "end": v(7.92, -1.6) * mm});
            skLineSegment(sketch, "E169", {"start": v(7.92, -1.6) * mm, "end": v(6.82, -1.6) * mm});
            skLineSegment(sketch, "E170", {"start": v(6.82, -1.6) * mm, "end": v(6.82, -3.15) * mm});
            skLineSegment(sketch, "E171", {"start": v(6.82, -3.15) * mm, "end": v(-6.88, -3.15) * mm});
            skLineSegment(sketch, "E172", {"start": v(-6.88, -3.15) * mm, "end": v(-6.88, -1.6) * mm});
            skLineSegment(sketch, "E173", {"start": v(-6.88, -1.6) * mm, "end": v(-7.98, -1.6) * mm});
            skLineSegment(sketch, "E174", {"start": v(-7.98, -1.6) * mm, "end": v(-7.98, 1.6) * mm});
            skSolve(sketch);
        }
        {
            var Q0;
            Q0=makeQuery(id+"F17.imprint","IMPRINT",FACE,{"disambiguationData":[TD([[makeQuery(id+"F17.imprint","IMPRINT",EDGE,{"derivedFrom":sQuery(id+"F17.wireOp",EDGE,"E163")}),-1.0]])]});
            extrude(context, id + "F18", {"entities" : qUnion([Q0]), "endBound" : BoundingType.SYMMETRIC, "depth" : 1.3 * mm, "offsetDistance" : 25 * mm});
        }
        {
            var Q0;
            Q0=qCreatedBy(makeId("Front.planeOp"),FACE);
            var sketch = newSketch(context, id + "F19", { "sketchPlane" : qUnion([Q0])});
            skLineSegment(sketch, "E175.bottom", {"start": v(0.12, 0.08) * mm, "end": v(-0.12, 0.07) * mm});
            skLineSegment(sketch, "E175.top", {"start": v(0.13, -0.07) * mm, "end": v(-0.12, -0.08) * mm});
            skLineSegment(sketch, "E175.left", {"start": v(0.12, 0.08) * mm, "end": v(0.12, -0.07) * mm});
            skLineSegment(sketch, "E175.right", {"start": v(-0.12, 0.07) * mm, "end": v(-0.12, -0.07) * mm});
            skPoint(sketch, "E175.middle", {"position": v(0, 0) * mm});
            skSolve(sketch);
        }
        {
            var Q0;
            Q0=qCreatedBy(makeId("Right.planeOp"),FACE);
            var sketch = newSketch(context, id + "F20", { "sketchPlane" : qUnion([Q0])});
            skLineSegment(sketch, "E176", {"start": v(0, 0) * mm, "end": v(0.55, 0) * mm});
            skLineSegment(sketch, "E177", {"start": v(0.55, 0) * mm, "end": v(0.75, -1.47) * mm});
            skLineSegment(sketch, "E178", {"start": v(0.75, -1.47) * mm, "end": v(1.7, -1.55) * mm});
            skSolve(sketch);
        }
        {
            var Q0;
            Q0=qCreatedBy(makeId("Right.planeOp"),FACE);
            var sketch = newSketch(context, id + "F21", { "sketchPlane" : qUnion([Q0])});
            skLineSegment(sketch, "E179", {"start": v(0, 0) * mm, "end": v(-0.55, 0) * mm});
            skLineSegment(sketch, "E180", {"start": v(-0.55, 0) * mm, "end": v(-0.75, -1.47) * mm});
            skLineSegment(sketch, "E181", {"start": v(-0.75, -1.47) * mm, "end": v(-1.7, -1.55) * mm});
            skSolve(sketch);
        }
        {
            var Q0;
            Q0=makeQuery(id+"F19.imprint","IMPRINT",FACE,{"disambiguationData":[TD([[makeQuery(id+"F19.imprint","IMPRINT",EDGE,{"derivedFrom":sQuery(id+"F19.wireOp",EDGE,"E175.bottom")}),1.0]])]});
            var Q1;
            Q1=sQuery(id+"F20.wireOp",EDGE,"E176");
            var Q2;
            Q2=sQuery(id+"F20.wireOp",EDGE,"E177");
            var Q3;
            Q3=sQuery(id+"F20.wireOp",EDGE,"E178");
            sweep(context, id + "F22", {"profiles" : qUnion([Q0]), "path" : qUnion([Q1, Q2, Q3])});
        }
        {
            var Q0;
            Q0=makeQuery(id+"F19.imprint","IMPRINT",FACE,{"disambiguationData":[TD([[makeQuery(id+"F19.imprint","IMPRINT",EDGE,{"derivedFrom":sQuery(id+"F19.wireOp",EDGE,"E175.bottom")}),1.0]])]});
            var Q1;
            Q1=sQuery(id+"F21.wireOp",EDGE,"E179");
            var Q2;
            Q2=sQuery(id+"F21.wireOp",EDGE,"E180");
            var Q3;
            Q3=sQuery(id+"F21.wireOp",EDGE,"E181");
            sweep(context, id + "F23", {"profiles" : qUnion([Q0]), "path" : qUnion([Q1, Q2, Q3])});
        }
        {
            var Q0;
            Q0=makeQuery(id+"F23.opSweep","MID_CAP_EDGE",EDGE,{"disambiguationData":[OSD([sQuery(id+"F19.wireOp",EDGE,"E175.bottom"),sQuery(id+"F21.wireOp",VERTEX,"E181.start")])],"capPos":2.0});
            var Q1;
            Q1=makeQuery(id+"F23.opSweep","MID_CAP_EDGE",EDGE,{"disambiguationData":[OSD([sQuery(id+"F19.wireOp",EDGE,"E175.bottom"),sQuery(id+"F21.wireOp",VERTEX,"E180.start")])],"capPos":1.0});
            var Q2;
            Q2=makeQuery(id+"F23.opSweep","MID_CAP_EDGE",EDGE,{"disambiguationData":[OSD([sQuery(id+"F19.wireOp",EDGE,"E175.top"),sQuery(id+"F21.wireOp",VERTEX,"E180.start")])],"capPos":1.0});
            var Q3;
            Q3=makeQuery(id+"F23.opSweep","MID_CAP_EDGE",EDGE,{"disambiguationData":[OSD([sQuery(id+"F19.wireOp",EDGE,"E175.top"),sQuery(id+"F21.wireOp",VERTEX,"E181.start")])],"capPos":2.0});
            var Q4;
            Q4=makeQuery(id+"F22.opSweep","MID_CAP_EDGE",EDGE,{"disambiguationData":[OSD([sQuery(id+"F19.wireOp",EDGE,"E175.bottom"),sQuery(id+"F20.wireOp",VERTEX,"E178.start")])],"capPos":2.0});
            var Q5;
            Q5=makeQuery(id+"F22.opSweep","MID_CAP_EDGE",EDGE,{"disambiguationData":[OSD([sQuery(id+"F19.wireOp",EDGE,"E175.bottom"),sQuery(id+"F20.wireOp",VERTEX,"E177.start")])],"capPos":1.0});
            var Q6;
            Q6=makeQuery(id+"F22.opSweep","MID_CAP_EDGE",EDGE,{"disambiguationData":[OSD([sQuery(id+"F19.wireOp",EDGE,"E175.top"),sQuery(id+"F20.wireOp",VERTEX,"E178.start")])],"capPos":2.0});
            var Q7;
            Q7=makeQuery(id+"F22.opSweep","MID_CAP_EDGE",EDGE,{"disambiguationData":[OSD([sQuery(id+"F19.wireOp",EDGE,"E175.top"),sQuery(id+"F20.wireOp",VERTEX,"E177.start")])],"capPos":1.0});
            fillet(context, id + "F24", {"entities" : qUnion([Q0, Q1, Q2, Q3, Q4, Q5, Q6, Q7]), "radius" : 0.15 * mm, "tangentPropagation" : true, "allowEdgeOverflow" : false});
        }
        {
            var Q0;
            {var subQ0=sQuery(id+"F0.wireOp",EDGE,"E0.top");var subQ1=sQuery(id+"F0.wireOp",EDGE,"E0.bottom");var subQ2=sQuery(id+"F12.wireOp",EDGE,"E134");Q0=makeQuery(id+"F14.boolean.opBoolean","COPY",EDGE,{"disambiguationData":[TD([makeQuery(id+"F1.opExtrude","SWEPT_FACE",FACE,{"disambiguationData":[OSD([subQ0])]})])],"derivedFrom":makeQuery(id+"F14.opExtrude","SWEPT_EDGE",EDGE,{"disambiguationData":[OSD([subQ1,subQ2,sQuery(id+"F12.wireOp",EDGE,"E138")])]})});}
            var Q1;
            {var subQ0=sQuery(id+"F0.wireOp",EDGE,"E0.bottom");var subQ1=sQuery(id+"F12.wireOp",EDGE,"E134");Q1=makeQuery(id+"F14.boolean.opBoolean","COPY",EDGE,{"disambiguationData":[TD([makeQuery(id+"F1.opExtrude","SWEPT_FACE",FACE,{"disambiguationData":[OSD([subQ0])]})])],"derivedFrom":makeQuery(id+"F14.opExtrude","SWEPT_EDGE",EDGE,{"disambiguationData":[OSD([subQ0,subQ1,sQuery(id+"F12.wireOp",EDGE,"E138")])]})});}
            var Q2;
            Q2=makeQuery(id+"F16.boolean.opBoolean","COPY",EDGE,{"derivedFrom":makeQuery(id+"F16.opExtrude","SWEPT_EDGE",EDGE,{"disambiguationData":[OSD([sQuery(id+"F15.wireOp",EDGE,"E157.MirrorCS"),sQuery(id+"F15.wireOp",EDGE,"E158.MirrorCS")])]})});
            var Q3;
            {var subQ0=sQuery(id+"F0.wireOp",EDGE,"E0.bottom");Q3=makeQuery(id+"F16.boolean.opBoolean","INTERSECT",EDGE,{"derivedFrom":[makeQuery(id+"F14.boolean.opBoolean","COPY",FACE,{"disambiguationData":[TD([makeQuery(id+"F1.opExtrude","SWEPT_FACE",FACE,{"disambiguationData":[OSD([subQ0])]})])],"derivedFrom":makeQuery(id+"F14.opExtrude","SWEPT_FACE",FACE,{"disambiguationData":[OSD([sQuery(id+"F12.wireOp",EDGE,"E134")])]})}),makeQuery(id+"F16.opExtrude","SWEPT_FACE",FACE,{"disambiguationData":[OSD([sQuery(id+"F15.wireOp",EDGE,"E157.MirrorCS")])]})]});}
            var Q4;
            {var subQ1=sQuery(id+"F0.wireOp",EDGE,"E0.bottom");Q4=makeQuery(id+"F16.boolean.opBoolean","INTERSECT",EDGE,{"derivedFrom":[makeQuery(id+"F14.boolean.opBoolean","COPY",FACE,{"disambiguationData":[TD([makeQuery(id+"F1.opExtrude","SWEPT_FACE",FACE,{"disambiguationData":[OSD([subQ1])]})])],"derivedFrom":makeQuery(id+"F14.opExtrude","SWEPT_FACE",FACE,{"disambiguationData":[OSD([sQuery(id+"F12.wireOp",EDGE,"E135.MirrorCS")])]})}),makeQuery(id+"F16.opExtrude","SWEPT_FACE",FACE,{"disambiguationData":[OSD([sQuery(id+"F15.wireOp",EDGE,"E160.MirrorCS")])]})]});}
            var Q5;
            {var subQ0=sQuery(id+"F0.wireOp",EDGE,"E0.bottom");var subQ1=sQuery(id+"F12.wireOp",EDGE,"E136.MirrorCS");Q5=makeQuery(id+"F14.boolean.opBoolean","COPY",EDGE,{"disambiguationData":[TD([makeQuery(id+"F1.opExtrude","SWEPT_FACE",FACE,{"disambiguationData":[OSD([subQ0])]})])],"derivedFrom":makeQuery(id+"F14.opExtrude","SWEPT_EDGE",EDGE,{"disambiguationData":[OSD([subQ0,subQ1,sQuery(id+"F12.wireOp",EDGE,"E143.MirrorCS")])]})});}
            var Q6;
            {var subQ0=sQuery(id+"F0.wireOp",EDGE,"E1");var subQ1=sQuery(id+"F0.wireOp",EDGE,"E0.bottom");var subQ2=sQuery(id+"F12.wireOp",EDGE,"E136.MirrorCS");Q6=makeQuery(id+"F14.boolean.opBoolean","COPY",EDGE,{"disambiguationData":[TD([makeQuery(id+"F1.opExtrude","SWEPT_FACE",FACE,{"disambiguationData":[OSD([subQ0])]})])],"derivedFrom":makeQuery(id+"F14.opExtrude","SWEPT_EDGE",EDGE,{"disambiguationData":[OSD([subQ1,subQ2,sQuery(id+"F12.wireOp",EDGE,"E143.MirrorCS")])]})});}
            var Q7;
            Q7=makeQuery(id+"F1.opExtrude","CAP_EDGE",EDGE,{"disambiguationData":[OSD([sQuery(id+"F0.wireOp",EDGE,"E1")])],"isStart":false});
            var Q8;
            Q8=makeQuery(id+"F14.boolean.opBoolean","INTERSECT",EDGE,{"derivedFrom":[makeQuery(id+"F1.opExtrude","SWEPT_FACE",FACE,{"disambiguationData":[OSD([sQuery(id+"F0.wireOp",EDGE,"E1")])]}),makeQuery(id+"F14.opExtrude","SWEPT_FACE",FACE,{"disambiguationData":[OSD([sQuery(id+"F12.wireOp",EDGE,"E136.MirrorCS")])]})]});
            var Q9;
            Q9=makeQuery(id+"F14.boolean.opBoolean","INTERSECT",EDGE,{"derivedFrom":[makeQuery(id+"F1.opExtrude","SWEPT_FACE",FACE,{"disambiguationData":[OSD([sQuery(id+"F0.wireOp",EDGE,"E1")])]}),makeQuery(id+"F14.opExtrude","SWEPT_FACE",FACE,{"disambiguationData":[OSD([sQuery(id+"F12.wireOp",EDGE,"E137.MirrorCS")])]})]});
            var Q10;
            {var subQ0=sQuery(id+"F0.wireOp",EDGE,"E0.bottom");Q10=makeQuery(id+"F16.boolean.opBoolean","INTERSECT",EDGE,{"derivedFrom":[makeQuery(id+"F14.boolean.opBoolean","COPY",FACE,{"disambiguationData":[TD([makeQuery(id+"F1.opExtrude","SWEPT_FACE",FACE,{"disambiguationData":[OSD([subQ0])]})])],"derivedFrom":makeQuery(id+"F14.opExtrude","SWEPT_FACE",FACE,{"disambiguationData":[OSD([sQuery(id+"F12.wireOp",EDGE,"E136.MirrorCS")])]})}),makeQuery(id+"F16.opExtrude","SWEPT_FACE",FACE,{"disambiguationData":[OSD([sQuery(id+"F15.wireOp",EDGE,"E157.MirrorCS")])]})]});}
            var Q11;
            {var subQ1=sQuery(id+"F0.wireOp",EDGE,"E0.bottom");Q11=makeQuery(id+"F16.boolean.opBoolean","INTERSECT",EDGE,{"derivedFrom":[makeQuery(id+"F14.boolean.opBoolean","COPY",FACE,{"disambiguationData":[TD([makeQuery(id+"F1.opExtrude","SWEPT_FACE",FACE,{"disambiguationData":[OSD([subQ1])]})])],"derivedFrom":makeQuery(id+"F14.opExtrude","SWEPT_FACE",FACE,{"disambiguationData":[OSD([sQuery(id+"F12.wireOp",EDGE,"E137.MirrorCS")])]})}),makeQuery(id+"F16.opExtrude","SWEPT_FACE",FACE,{"disambiguationData":[OSD([sQuery(id+"F15.wireOp",EDGE,"E160.MirrorCS")])]})]});}
            var Q12;
            Q12=makeQuery(id+"F16.boolean.opBoolean","INTERSECT",EDGE,{"derivedFrom":[makeQuery(id+"F1.opExtrude","SWEPT_FACE",FACE,{"disambiguationData":[OSD([sQuery(id+"F0.wireOp",EDGE,"E1")])]}),makeQuery(id+"F16.opExtrude","SWEPT_FACE",FACE,{"disambiguationData":[OSD([sQuery(id+"F15.wireOp",EDGE,"E153")])]})]});
            var Q13;
            Q13=makeQuery(id+"F16.boolean.opBoolean","INTERSECT",EDGE,{"derivedFrom":[makeQuery(id+"F1.opExtrude","SWEPT_FACE",FACE,{"disambiguationData":[OSD([sQuery(id+"F0.wireOp",EDGE,"E1")])]}),makeQuery(id+"F16.opExtrude","SWEPT_FACE",FACE,{"disambiguationData":[OSD([sQuery(id+"F15.wireOp",EDGE,"E156.MirrorCS")])]})]});
            var Q14;
            Q14=makeQuery(id+"F16.boolean.opBoolean","COPY",EDGE,{"derivedFrom":makeQuery(id+"F16.opExtrude","SWEPT_EDGE",EDGE,{"disambiguationData":[OSD([sQuery(id+"F0.wireOp",EDGE,"E0.right"),sQuery(id+"F15.wireOp",EDGE,"E152"),sQuery(id+"F15.wireOp",EDGE,"E153")])]})});
            var Q15;
            {var subQ0=sQuery(id+"F0.wireOp",EDGE,"E0.top");Q15=makeQuery(id+"F16.boolean.opBoolean","INTERSECT",EDGE,{"derivedFrom":[makeQuery(id+"F14.boolean.opBoolean","COPY",FACE,{"disambiguationData":[TD([makeQuery(id+"F1.opExtrude","SWEPT_FACE",FACE,{"disambiguationData":[OSD([subQ0])]})])],"derivedFrom":makeQuery(id+"F14.opExtrude","SWEPT_FACE",FACE,{"disambiguationData":[OSD([sQuery(id+"F12.wireOp",EDGE,"E134")])]})}),makeQuery(id+"F16.opExtrude","SWEPT_FACE",FACE,{"disambiguationData":[OSD([sQuery(id+"F15.wireOp",EDGE,"E153")])]})]});}
            var Q16;
            {var subQ1=sQuery(id+"F0.wireOp",EDGE,"E0.top");Q16=makeQuery(id+"F16.boolean.opBoolean","INTERSECT",EDGE,{"derivedFrom":[makeQuery(id+"F14.boolean.opBoolean","COPY",FACE,{"disambiguationData":[TD([makeQuery(id+"F1.opExtrude","SWEPT_FACE",FACE,{"disambiguationData":[OSD([subQ1])]})])],"derivedFrom":makeQuery(id+"F14.opExtrude","SWEPT_FACE",FACE,{"disambiguationData":[OSD([sQuery(id+"F12.wireOp",EDGE,"E135.MirrorCS")])]})}),makeQuery(id+"F16.opExtrude","SWEPT_FACE",FACE,{"disambiguationData":[OSD([sQuery(id+"F15.wireOp",EDGE,"E156.MirrorCS")])]})]});}
            fillet(context, id + "F25", {"entities" : qUnion([Q0, Q1, Q2, Q3, Q4, Q5, Q6, Q7, Q8, Q9, Q10, Q11, Q12, Q13, Q14, Q15, Q16]), "radius" : 0.1 * mm, "tangentPropagation" : true, "allowEdgeOverflow" : false});
        }
        {
            var Q0;
            Q0=makeQuery(id+"F7.boolean.opBoolean","COPY",EDGE,{"derivedFrom":makeQuery(id+"F7.opExtrude","CAP_EDGE",EDGE,{"disambiguationData":[OSD([sQuery(id+"F6.wireOp",EDGE,"E41")])],"isStart":false})});
            var Q1;
            Q1=makeQuery(id+"F7.boolean.opBoolean","COPY",EDGE,{"derivedFrom":makeQuery(id+"F7.opExtrude","CAP_EDGE",EDGE,{"disambiguationData":[OSD([sQuery(id+"F6.wireOp",EDGE,"E43.MirrorCS")])],"isStart":false})});
            var Q2;
            Q2=makeQuery(id+"F5.boolean.opBoolean","COPY",EDGE,{"derivedFrom":makeQuery(id+"F5.opExtrude","CAP_EDGE",EDGE,{"disambiguationData":[OSD([sQuery(id+"F4.wireOp",EDGE,"E37.MirrorCS")])],"isStart":false})});
            var Q3;
            Q3=makeQuery(id+"F5.boolean.opBoolean","COPY",EDGE,{"derivedFrom":makeQuery(id+"F5.opExtrude","CAP_EDGE",EDGE,{"disambiguationData":[OSD([sQuery(id+"F4.wireOp",EDGE,"E35")])],"isStart":false})});
            fillet(context, id + "F26", {"entities" : qUnion([Q0, Q1, Q2, Q3]), "radius" : 0.5 * mm, "tangentPropagation" : true, "allowEdgeOverflow" : false});
        }
        {
            var Q0;
            Q0=makeQuery(id+"F8.imprint","IMPRINT",FACE,{"disambiguationData":[TD([[makeQuery(id+"F8.imprint","IMPRINT",EDGE,{"derivedFrom":sQuery(id+"F8.wireOp",EDGE,"E46")}),1.0]])]});
            extrude(context, id + "F27", {"entities" : qUnion([Q0]), "operationType" : NewBodyOperationType.REMOVE, "oppositeDirection" : true, "depth" : 0.15 * mm, "offsetDistance" : 25 * mm});
        }
        {
            var Q0;
            Q0=makeQuery(id+"F27.boolean.opBoolean","COPY",EDGE,{"derivedFrom":makeQuery(id+"F27.opExtrude","CAP_EDGE",EDGE,{"disambiguationData":[OSD([sQuery(id+"F8.wireOp",EDGE,"E46")])],"isStart":true})});
            var Q1;
            Q1=makeQuery(id+"F27.boolean.opBoolean","COPY",EDGE,{"derivedFrom":makeQuery(id+"F27.opExtrude","CAP_EDGE",EDGE,{"disambiguationData":[OSD([sQuery(id+"F8.wireOp",EDGE,"E46")])],"isStart":false})});
            chamfer(context, id + "F28", {"entities" : qUnion([Q0, Q1]), "width" : 0.05 * mm, "tangentPropagation" : true});
        }
    });
